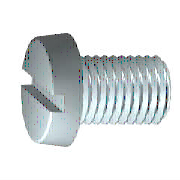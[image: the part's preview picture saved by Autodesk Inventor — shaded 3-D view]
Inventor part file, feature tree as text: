
AUTODESK INVENTOR PART (.ipt)
format: ipt  version: 2022 (Build 260153000, 153)  size: 187,904 bytes
history: native  units: mm (DEFAULTED — no unit token found)
features: sketch x2, other x1, extrude x1, plane x1
ambient origin geometry x7: Origin, YZ Plane, XZ Plane, X Axis, Y Axis, Z Axis, Center Point
bodies: Solid1 (feature_tree)
feature tree (5):
  other  "Базовый элемент"
  sketch  "Эскиз2"
  extrude  "Паз"  Depth=10.0mm
  plane  "Work Plane1"
  sketch  "Эскиз1"
